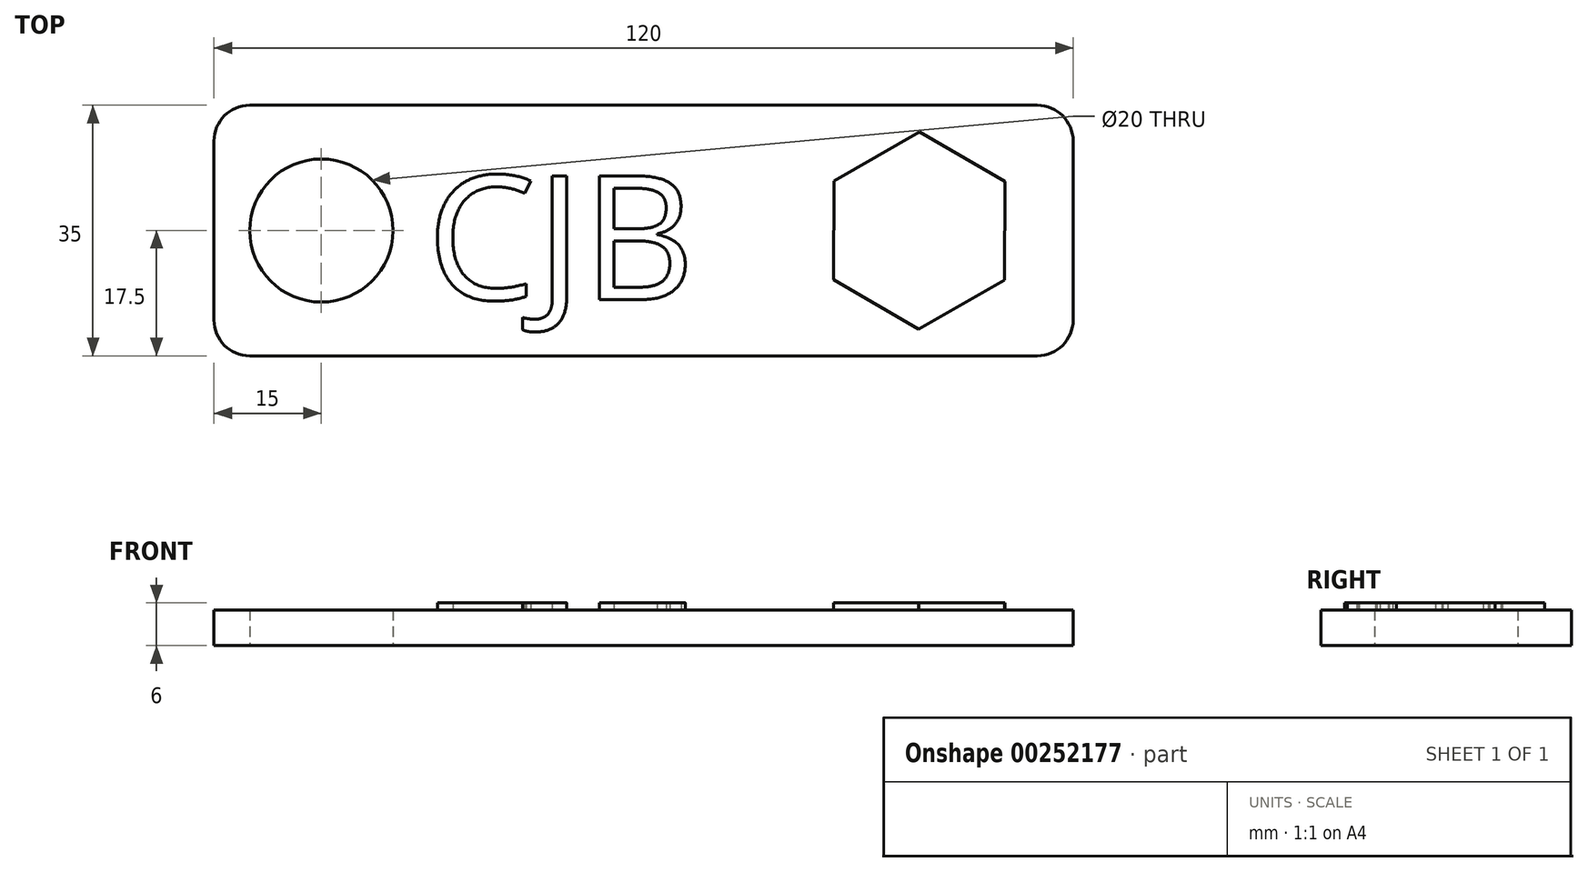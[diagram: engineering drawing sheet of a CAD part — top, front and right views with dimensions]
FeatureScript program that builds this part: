
annotation { "Feature Type Name" : "Feature", "Feature Type Description" : "" }
export const myFeature = defineFeature(function(context is Context, id is Id, definition is map)
    precondition{}
    {
        {
            var Q0;
            Q0=qCreatedBy(makeId("Top.planeOp"),FACE);
            var sketch = newSketch(context, id + "F0", { "sketchPlane" : qUnion([Q0])});
            skLineSegment(sketch, "E0.bottom", {"start": v(-60, 17.5) * mm, "end": v(60, 17.5) * mm});
            skLineSegment(sketch, "E0.top", {"start": v(-60, -17.5) * mm, "end": v(60, -17.5) * mm});
            skLineSegment(sketch, "E0.left", {"start": v(-60, 17.5) * mm, "end": v(-60, -17.5) * mm});
            skLineSegment(sketch, "E0.right", {"start": v(60, 17.5) * mm, "end": v(60, -17.5) * mm});
            skPoint(sketch, "E0.middle", {"position": v(0, 0) * mm});
            skCircle(sketch, "E1", {"center": v(-45, 0) * mm, "radius": 10 * mm});
            skSolve(sketch);
        }
        {
            var Q0;
            Q0=makeQuery(id+"F0.imprint","IMPRINT",FACE,{"disambiguationData":[TD([[makeQuery(id+"F0.imprint","IMPRINT",EDGE,{"derivedFrom":sQuery(id+"F0.wireOp",EDGE,"E0.bottom")}),-1.0]])]});
            extrude(context, id + "F1", {"entities" : qUnion([Q0]), "depth" : 5 * mm});
        }
        {
            var Q0;
            Q0=makeQuery(id+"F1.opExtrude","SWEPT_EDGE",EDGE,{"disambiguationData":[OSD([sQuery(id+"F0.wireOp",EDGE,"E0.top"),sQuery(id+"F0.wireOp",EDGE,"E0.right")])]});
            var Q1;
            Q1=makeQuery(id+"F1.opExtrude","SWEPT_EDGE",EDGE,{"disambiguationData":[OSD([sQuery(id+"F0.wireOp",EDGE,"E0.bottom"),sQuery(id+"F0.wireOp",EDGE,"E0.right")])]});
            var Q2;
            Q2=makeQuery(id+"F1.opExtrude","SWEPT_EDGE",EDGE,{"disambiguationData":[OSD([sQuery(id+"F0.wireOp",EDGE,"E0.top"),sQuery(id+"F0.wireOp",EDGE,"E0.left")])]});
            var Q3;
            Q3=makeQuery(id+"F1.opExtrude","SWEPT_EDGE",EDGE,{"disambiguationData":[OSD([sQuery(id+"F0.wireOp",EDGE,"E0.bottom"),sQuery(id+"F0.wireOp",EDGE,"E0.left")])]});
            fillet(context, id + "F2", {"entities" : qUnion([Q0, Q1, Q2, Q3]), "radius" : 5 * mm, "tangentPropagation" : true, "allowEdgeOverflow" : false});
        }
        {
            var Q0;
            Q0=makeQuery(id+"F1.opExtrude","CAP_FACE",FACE,{"disambiguationData":[OSD([sQuery(id+"F0.wireOp",EDGE,"E0.bottom"),sQuery(id+"F0.wireOp",EDGE,"E0.top"),sQuery(id+"F0.wireOp",EDGE,"E0.left"),sQuery(id+"F0.wireOp",EDGE,"E0.right"),sQuery(id+"F0.wireOp",EDGE,"E1")])],"isStart":false});
            var sketch = newSketch(context, id + "F3", { "sketchPlane" : qUnion([Q0])});
            skText(sketch, "E2", { "text": "CJB", "fontName": "OpenSans-Regular.ttf"});
            skCircle(sketch, "E3.cCircle", {"center": v(38.49, 0) * mm, "radius": 11.93 * mm, "construction": true});
            skLineSegment(sketch, "E3.0", {"start": v(26.58, 6.94) * mm, "end": v(38.55, 13.78) * mm});
            skLineSegment(sketch, "E3.1", {"start": v(38.55, 13.78) * mm, "end": v(50.45, 6.84) * mm});
            skLineSegment(sketch, "E3.2", {"start": v(50.45, 6.84) * mm, "end": v(50.4, -6.94) * mm});
            skLineSegment(sketch, "E3.3", {"start": v(50.4, -6.94) * mm, "end": v(38.43, -13.78) * mm});
            skLineSegment(sketch, "E3.4", {"start": v(38.43, -13.78) * mm, "end": v(26.52, -6.84) * mm});
            skLineSegment(sketch, "E3.5", {"start": v(26.52, -6.84) * mm, "end": v(26.58, 6.94) * mm});
            skPoint(sketch, "E3.0.midPoint", {"position": v(32.57, 10.36) * mm});
            const initialGuessF3  = {"E2": [-0.03027, -0.00963, 1, 0, 0.01743]};
            skSetInitialGuess(sketch, initialGuessF3);
            skSolve(sketch);
        }
        {
            var Q0;
            Q0 = qSketchRegion(id + "F3", true);
            extrude(context, id + "F4", {"entities" : qUnion([Q0]), "operationType" : NewBodyOperationType.ADD, "depth" : 1 * mm});
        }
    });
